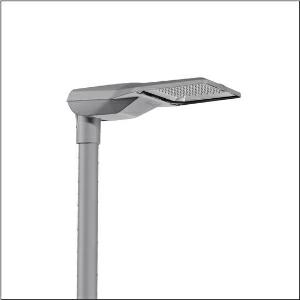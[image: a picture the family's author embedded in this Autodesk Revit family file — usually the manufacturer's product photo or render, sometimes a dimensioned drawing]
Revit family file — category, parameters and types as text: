
# Revit family: streetlight_sl_21_iq_midi___st0_5a_5xe3b41d08mb_eec4
name_source: partatom
category: Lighting Fixtures
units: mm (PartAtom-declared; Revit-internal decimal feet)

## family parameters
Cut with Voids When Loaded = No
Host = Face
Light Source = No
Part Type = Normal
Room Calculation Point = No
Round Connector Dimension = Use Diameter
Shared = No

## types (1)
- --- (1 x LED, 20360 lm, 146.7 W, 4000K)
    Apparent Load = 147 VA
    CIE Flux Codes = 41 75 97 100 100
    Color Rendering = 70
    Color Temperature = 4000K
    Default Elevation = 1800 mm
    Description = Streetlight SL 21 iQ midi, mast luminaire, primary light control with lens, of PMMA, primary optical cover: cover, of toughened safety glass, transparent, light distribution: ST0.5a, light emission: direct distribution, primary light characteristic: asymmetric, installation type: post-top, side-entry, LED, High Power LED, rated luminous flux: 20.360lm, luminous efficacy: 139lm/W, light colour: 740, colour temperature: 4000K, control: Auto-Match, Temp-Guard, Lumen-Switch, Night-Set, Smart-Wire, Light-Fading, Desk-Remote (wireless, voltage-free reading and setting of iQ features in the workshop via application-optimized NFC function/RFID function), optimised constant luminous flux control (CLO 2.0), pre-setting: linear dimming characteristic, mains connection: 230..240V, AC, 50/60Hz, start of lifetime: 147W, end of service life: 161W, reduction: 62W, luminaire housing, of diecast aluminium, powder-coated, Siteco® metallic grey (DB 702S), corrosivity category C5 mid according to DIN EN ISO 12944, please order mast flange separately, inclination adjustable: 0°, 5°, 10°, 15°, sealing non-destructively replaceable, multi-level sealing system, length: 644mm, width: 335mm, height: 110mm, mast flange for spigot size: 42mm (side-entry): 5XC10008XM4, 60/48mm (side-entry/post-top): 5XC10108XM2, 76/60mm (side-entry/post-top): 5XC10108XM1, protection rating (complete): IP66, insulation class (complete): insulation class II (safety insulation), certification: CE, ENEC, ENEC+, VDE, impact resistance: IK09, permissible operating ambient temperature for outdoor applications: -40..+50°C, standard-compliant lighting for roads and squares, packaging unit: 1 piece

Light Distribution: ST0.5a
    Height = 111 mm
    Lamp = 1 x LED
    Lamp Light Flux = 20360 lm
    Lamp Power = 146.7 W
    Lamp count = 1
    Length = 644 mm
    Luminous efficacy = 139 lm/W
    Manufacturer = Siteco
    ModVariant = No
    Model = 5XE3B41D08MB
    Number of Poles = 1
    OnlyDefault = Yes
    Power Factor = 1
    Product Name = Streetlight SL 21 iQ midi | ST0.5a
    Product group = mast luminaire | pylon top
    ProductGroupID = 6100
    Protection Class = Protection class II
    Protection Degree = IP 66
    RLX_Detail_Level = 1
    RLX_Emergency_Light_Flux = 0 lm
    RLX_Emergency_Type = 0
    RLX_Emergency_Type_DB = No
    RlxData = <blob elided: 101901 chars, md5=c0b3bbd8>
    Socket = socket
    Standby Power = 0 W
    System Light Flux = 20360 lm
    System Power = 147 W
    Type Comments = factory setting: luminous flux: 100 % | dim-lin: 254 | 753 mA
    Type Image = l_1004298.jpg
    URL = http://relux.com
    VarID = @adj_164481
    Voltage = 0 V
    Weight = 0.00 kg
    Width = 336 mm

## geometry (parser evidence)
native form markers: Blend x4, Sweep x11
no freeform markers — native parametric forms only
